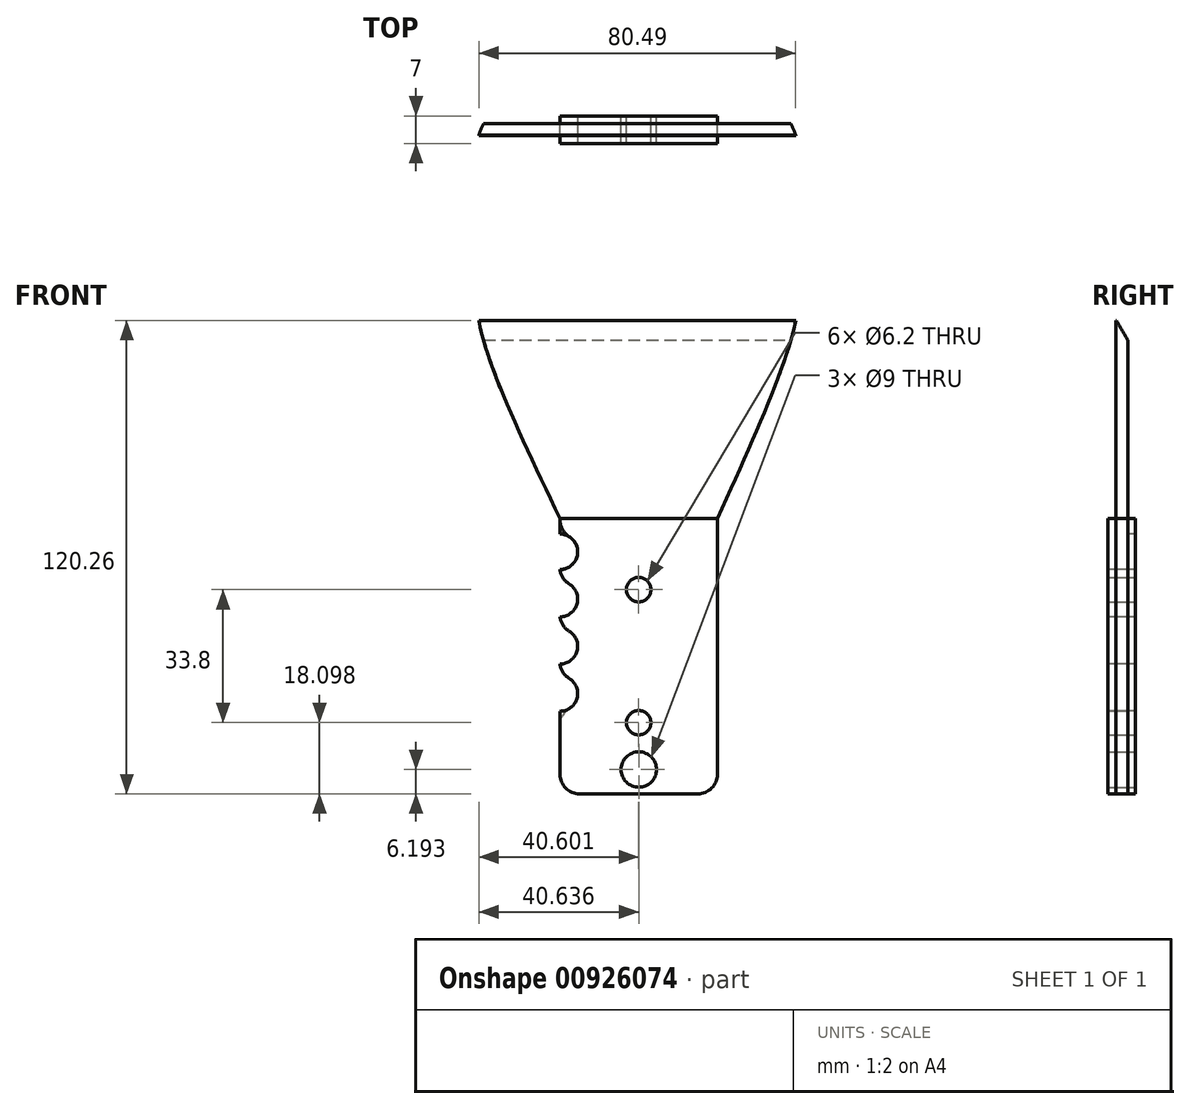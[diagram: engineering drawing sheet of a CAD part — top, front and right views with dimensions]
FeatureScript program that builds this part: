
annotation { "Feature Type Name" : "Feature", "Feature Type Description" : "" }
export const myFeature = defineFeature(function(context is Context, id is Id, definition is map)
    precondition{}
    {
        {
            var Q0;
            Q0=qCreatedBy(makeId("Front.planeOp"),FACE);
            var sketch = newSketch(context, id + "F0", { "sketchPlane" : qUnion([Q0])});
            skLineSegment(sketch, "E0.bottom", {"start": v(-37.72, -65.67) * mm, "end": v(2.28, -65.67) * mm});
            skLineSegment(sketch, "E0.top", {"start": v(-37.72, 4.33) * mm, "end": v(2.28, 4.33) * mm});
            skLineSegment(sketch, "E0.left", {"start": v(-37.72, -65.67) * mm, "end": v(-37.72, 4.33) * mm});
            skLineSegment(sketch, "E0.right", {"start": v(2.28, -65.67) * mm, "end": v(2.28, 4.33) * mm});
            skFitSpline(sketch, "E1", {"points": [v(-37.72, 4.33) * mm, v(-58.32, 54.6) * mm, v(-57.84, 68.97) * mm], "startDerivative": vector(-41.97, 87.3) * mm, "endDerivative": vector(6.95, 36.57) * mm});
            skFitSpline(sketch, "E2", {"points": [v(2.28, 4.33) * mm, v(22.17, 54.6) * mm, v(22.41, 68) * mm], "startDerivative": vector(39.5, 86.98) * mm, "endDerivative": vector(-4.12, 34.53) * mm});
            skLineSegment(sketch, "E3", {"start": v(-58.32, 54.6) * mm, "end": v(22.17, 54.6) * mm});
            skSolve(sketch);
        }
        {
            var Q0;
            Q0 = qSketchRegion(id + "F0", true);
            extrude(context, id + "F1", {"entities" : qUnion([Q0]), "depth" : 3 * mm, "offsetDistance" : 25 * mm});
        }
        {
            var Q0;
            Q0=makeQuery(id+"F1.opExtrude","CAP_EDGE",EDGE,{"disambiguationData":[OSD([sQuery(id+"F0.wireOp",EDGE,"E3")])],"isStart":true});
            chamfer(context, id + "F2", {"entities" : qUnion([Q0]), "chamferType" : ChamferType.OFFSET_ANGLE, "width" : 5 * mm, "oppositeDirection" : false, "angle" : 30 * degree, "tangentPropagation" : true});
        }
        {
            var Q0;
            Q0=makeQuery(id+"F1.opExtrude","SWEPT_EDGE",EDGE,{"disambiguationData":[OSD([sQuery(id+"F0.wireOp",EDGE,"E0.bottom"),sQuery(id+"F0.wireOp",EDGE,"E0.right")])]});
            var Q1;
            Q1=makeQuery(id+"F1.opExtrude","SWEPT_EDGE",EDGE,{"disambiguationData":[OSD([sQuery(id+"F0.wireOp",EDGE,"E0.bottom"),sQuery(id+"F0.wireOp",EDGE,"E0.left")])]});
            fillet(context, id + "F3", {"entities" : qUnion([Q0, Q1]), "radius" : 5 * mm, "tangentPropagation" : true, "allowEdgeOverflow" : false});
        }
        {
            var Q0;
            Q0=makeQuery(id+"F1.opExtrude","CAP_FACE",FACE,{"disambiguationData":[OSD([sQuery(id+"F0.wireOp",EDGE,"E0.bottom"),sQuery(id+"F0.wireOp",EDGE,"E0.left"),sQuery(id+"F0.wireOp",EDGE,"E0.right"),sQuery(id+"F0.wireOp",EDGE,"E1"),sQuery(id+"F0.wireOp",EDGE,"E2"),sQuery(id+"F0.wireOp",EDGE,"E3")])],"isStart":false});
            var sketch = newSketch(context, id + "F4", { "sketchPlane" : qUnion([Q0])});
            skLineSegment(sketch, "E4", {"start": v(-37.72, 4.33) * mm, "end": v(2.28, 4.33) * mm});
            skSolve(sketch);
        }
        {
            var Q0;
            Q0=makeQuery(id+"F4.imprint","IMPRINT",FACE,{"disambiguationData":[TD([[makeQuery(id+"F4.imprint","IMPRINT",EDGE,{"derivedFrom":sQuery(id+"F4.wireOp",EDGE,"E4")}),-1.0]])]});
            extrude(context, id + "F5", {"entities" : qUnion([Q0]), "depth" : 2 * mm, "offsetDistance" : 25 * mm});
        }
        {
            var Q0;
            Q0=makeQuery(id+"F1.opExtrude","CAP_FACE",FACE,{"disambiguationData":[OSD([sQuery(id+"F0.wireOp",EDGE,"E0.bottom"),sQuery(id+"F0.wireOp",EDGE,"E0.left"),sQuery(id+"F0.wireOp",EDGE,"E0.right"),sQuery(id+"F0.wireOp",EDGE,"E1"),sQuery(id+"F0.wireOp",EDGE,"E2"),sQuery(id+"F0.wireOp",EDGE,"E3")])],"isStart":true});
            var sketch = newSketch(context, id + "F6", { "sketchPlane" : qUnion([Q0])});
            skLineSegment(sketch, "E5", {"start": v(-2.28, 4.33) * mm, "end": v(37.72, 4.33) * mm});
            skSolve(sketch);
        }
        {
            var Q0;
            Q0=makeQuery(id+"F6.imprint","IMPRINT",FACE,{"disambiguationData":[TD([[makeQuery(id+"F6.imprint","IMPRINT",EDGE,{"derivedFrom":sQuery(id+"F6.wireOp",EDGE,"E5")}),-1.0]])]});
            extrude(context, id + "F7", {"entities" : qUnion([Q0]), "depth" : 2 * mm, "offsetDistance" : 25 * mm});
        }
        {
            var Q0;
            Q0=makeQuery(id+"F5.opExtrude","CAP_FACE",FACE,{"disambiguationData":[OSD([sQuery(id+"F0.wireOp",EDGE,"E0.bottom"),sQuery(id+"F0.wireOp",EDGE,"E0.left"),sQuery(id+"F0.wireOp",EDGE,"E0.right"),sQuery(id+"F0.wireOp",EDGE,"E1"),sQuery(id+"F0.wireOp",EDGE,"E2"),sQuery(id+"F0.wireOp",EDGE,"E3"),sQuery(id+"F4.wireOp",EDGE,"E4")])],"isStart":false});
            var sketch = newSketch(context, id + "F8", { "sketchPlane" : qUnion([Q0])});
            skCircle(sketch, "E6", {"center": v(-37.72, -4.17) * mm, "radius": 4.5 * mm});
            skCircle(sketch, "E7", {"center": v(-37.72, -16.17) * mm, "radius": 4.5 * mm});
            skCircle(sketch, "E8", {"center": v(-37.72, -28.17) * mm, "radius": 4.5 * mm});
            skCircle(sketch, "E9", {"center": v(-37.72, -40.17) * mm, "radius": 4.5 * mm});
            skSolve(sketch);
        }
        {
            var Q0;
            {var subQ0=sQuery(id+"F8.wireOp",EDGE,"E6");var subQ1=makeQuery(id+"F5.opExtrude","CAP_EDGE",EDGE,{"disambiguationData":[OSD([sQuery(id+"F0.wireOp",EDGE,"E0.left")])],"isStart":false});var subQ2=makeQuery(id+"F8.imprint","INTERSECT",VERTEX,{"disambiguationData":[OD(0.0)],"derivedFrom":[subQ1,subQ0]});Q0=makeQuery(id+"F8.imprint","IMPRINT",FACE,{"disambiguationData":[TD([[makeQuery(id+"F8.imprint","IMPRINT",EDGE,{"disambiguationData":[TD([[subQ2,1.0]])],"derivedFrom":subQ0}),1.0]])]});}
            var Q1;
            {var subQ0=sQuery(id+"F8.wireOp",EDGE,"E7");var subQ1=makeQuery(id+"F5.opExtrude","CAP_EDGE",EDGE,{"disambiguationData":[OSD([sQuery(id+"F0.wireOp",EDGE,"E0.left")])],"isStart":false});var subQ2=makeQuery(id+"F8.imprint","INTERSECT",VERTEX,{"disambiguationData":[OD(0.0)],"derivedFrom":[subQ1,subQ0]});Q1=makeQuery(id+"F8.imprint","IMPRINT",FACE,{"disambiguationData":[TD([[makeQuery(id+"F8.imprint","IMPRINT",EDGE,{"disambiguationData":[TD([[subQ2,1.0]])],"derivedFrom":subQ0}),1.0]])]});}
            var Q2;
            {var subQ0=sQuery(id+"F8.wireOp",EDGE,"E8");var subQ1=makeQuery(id+"F5.opExtrude","CAP_EDGE",EDGE,{"disambiguationData":[OSD([sQuery(id+"F0.wireOp",EDGE,"E0.left")])],"isStart":false});var subQ2=makeQuery(id+"F8.imprint","INTERSECT",VERTEX,{"disambiguationData":[OD(0.0)],"derivedFrom":[subQ1,subQ0]});Q2=makeQuery(id+"F8.imprint","IMPRINT",FACE,{"disambiguationData":[TD([[makeQuery(id+"F8.imprint","IMPRINT",EDGE,{"disambiguationData":[TD([[subQ2,-1.0]])],"derivedFrom":subQ0}),1.0]])]});}
            var Q3;
            {var subQ0=sQuery(id+"F8.wireOp",EDGE,"E9");var subQ1=makeQuery(id+"F5.opExtrude","CAP_EDGE",EDGE,{"disambiguationData":[OSD([sQuery(id+"F0.wireOp",EDGE,"E0.left")])],"isStart":false});var subQ2=makeQuery(id+"F8.imprint","INTERSECT",VERTEX,{"disambiguationData":[OD(0.0)],"derivedFrom":[subQ1,subQ0]});Q3=makeQuery(id+"F8.imprint","IMPRINT",FACE,{"disambiguationData":[TD([[makeQuery(id+"F8.imprint","IMPRINT",EDGE,{"disambiguationData":[TD([[subQ2,-1.0]])],"derivedFrom":subQ0}),1.0]])]});}
            extrude(context, id + "F9", {"entities" : qUnion([Q0, Q1, Q2, Q3]), "operationType" : NewBodyOperationType.REMOVE, "oppositeDirection" : true, "depth" : 25 * mm, "offsetDistance" : 25 * mm});
        }
        {
            var Q0;
            {var subQ0=sQuery(id+"F0.wireOp",EDGE,"E0.left");var subQ1=sQuery(id+"F8.wireOp",EDGE,"E6");Q0=makeQuery(id+"F9.boolean.opBoolean","COPY",EDGE,{"disambiguationData":[topologyDisambiguationEdgeConnected([makeQuery(id+"F5.opExtrude","SWEPT_FACE",FACE,{"disambiguationData":[OSD([subQ0])]})])],"derivedFrom":makeQuery(id+"F9.opExtrude","SWEPT_EDGE",EDGE,{"disambiguationData":[OSD([subQ0,subQ1]),TDD([makeQuery(id+"F8.imprint","INTERSECT",VERTEX,{"disambiguationData":[OD(0.0)],"derivedFrom":[makeQuery(id+"F5.opExtrude","CAP_EDGE",EDGE,{"disambiguationData":[OSD([subQ0])],"isStart":false}),subQ1]})])]})});}
            var Q1;
            {var subQ0=sQuery(id+"F0.wireOp",EDGE,"E0.left");var subQ1=sQuery(id+"F8.wireOp",EDGE,"E6");Q1=makeQuery(id+"F9.boolean.opBoolean","COPY",EDGE,{"disambiguationData":[topologyDisambiguationEdgeConnected([makeQuery(id+"F1.opExtrude","SWEPT_FACE",FACE,{"disambiguationData":[OSD([subQ0])]})])],"derivedFrom":makeQuery(id+"F9.opExtrude","SWEPT_EDGE",EDGE,{"disambiguationData":[OSD([subQ0,subQ1]),TDD([makeQuery(id+"F8.imprint","INTERSECT",VERTEX,{"disambiguationData":[OD(0.0)],"derivedFrom":[makeQuery(id+"F5.opExtrude","CAP_EDGE",EDGE,{"disambiguationData":[OSD([subQ0])],"isStart":false}),subQ1]})])]})});}
            var Q2;
            {var subQ0=sQuery(id+"F0.wireOp",EDGE,"E0.left");var subQ1=sQuery(id+"F8.wireOp",EDGE,"E6");Q2=makeQuery(id+"F9.boolean.opBoolean","COPY",EDGE,{"disambiguationData":[topologyDisambiguationEdgeConnected([makeQuery(id+"F7.opExtrude","SWEPT_FACE",FACE,{"disambiguationData":[OSD([subQ0])]})])],"derivedFrom":makeQuery(id+"F9.opExtrude","SWEPT_EDGE",EDGE,{"disambiguationData":[OSD([subQ0,subQ1]),TDD([makeQuery(id+"F8.imprint","INTERSECT",VERTEX,{"disambiguationData":[OD(0.0)],"derivedFrom":[makeQuery(id+"F5.opExtrude","CAP_EDGE",EDGE,{"disambiguationData":[OSD([subQ0])],"isStart":false}),subQ1]})])]})});}
            var Q3;
            {var subQ0=sQuery(id+"F0.wireOp",EDGE,"E0.left");var subQ1=sQuery(id+"F8.wireOp",EDGE,"E7");Q3=makeQuery(id+"F9.boolean.opBoolean","COPY",EDGE,{"disambiguationData":[topologyDisambiguationEdgeConnected([makeQuery(id+"F5.opExtrude","SWEPT_FACE",FACE,{"disambiguationData":[OSD([subQ0])]})])],"derivedFrom":makeQuery(id+"F9.opExtrude","SWEPT_EDGE",EDGE,{"disambiguationData":[OSD([subQ0,subQ1]),TDD([makeQuery(id+"F8.imprint","INTERSECT",VERTEX,{"disambiguationData":[OD(0.0)],"derivedFrom":[makeQuery(id+"F5.opExtrude","CAP_EDGE",EDGE,{"disambiguationData":[OSD([subQ0])],"isStart":false}),subQ1]})])]})});}
            var Q4;
            {var subQ0=sQuery(id+"F0.wireOp",EDGE,"E0.left");var subQ1=sQuery(id+"F8.wireOp",EDGE,"E7");Q4=makeQuery(id+"F9.boolean.opBoolean","COPY",EDGE,{"disambiguationData":[topologyDisambiguationEdgeConnected([makeQuery(id+"F1.opExtrude","SWEPT_FACE",FACE,{"disambiguationData":[OSD([subQ0])]})])],"derivedFrom":makeQuery(id+"F9.opExtrude","SWEPT_EDGE",EDGE,{"disambiguationData":[OSD([subQ0,subQ1]),TDD([makeQuery(id+"F8.imprint","INTERSECT",VERTEX,{"disambiguationData":[OD(0.0)],"derivedFrom":[makeQuery(id+"F5.opExtrude","CAP_EDGE",EDGE,{"disambiguationData":[OSD([subQ0])],"isStart":false}),subQ1]})])]})});}
            var Q5;
            {var subQ0=sQuery(id+"F0.wireOp",EDGE,"E0.left");var subQ1=sQuery(id+"F8.wireOp",EDGE,"E7");Q5=makeQuery(id+"F9.boolean.opBoolean","COPY",EDGE,{"disambiguationData":[topologyDisambiguationEdgeConnected([makeQuery(id+"F7.opExtrude","SWEPT_FACE",FACE,{"disambiguationData":[OSD([subQ0])]})])],"derivedFrom":makeQuery(id+"F9.opExtrude","SWEPT_EDGE",EDGE,{"disambiguationData":[OSD([subQ0,subQ1]),TDD([makeQuery(id+"F8.imprint","INTERSECT",VERTEX,{"disambiguationData":[OD(0.0)],"derivedFrom":[makeQuery(id+"F5.opExtrude","CAP_EDGE",EDGE,{"disambiguationData":[OSD([subQ0])],"isStart":false}),subQ1]})])]})});}
            var Q6;
            {var subQ0=sQuery(id+"F0.wireOp",EDGE,"E0.left");var subQ1=sQuery(id+"F8.wireOp",EDGE,"E8");Q6=makeQuery(id+"F9.boolean.opBoolean","COPY",EDGE,{"disambiguationData":[topologyDisambiguationEdgeConnected([makeQuery(id+"F7.opExtrude","SWEPT_FACE",FACE,{"disambiguationData":[OSD([subQ0])]})])],"derivedFrom":makeQuery(id+"F9.opExtrude","SWEPT_EDGE",EDGE,{"disambiguationData":[OSD([subQ0,subQ1]),TDD([makeQuery(id+"F8.imprint","INTERSECT",VERTEX,{"disambiguationData":[OD(1.0)],"derivedFrom":[makeQuery(id+"F5.opExtrude","CAP_EDGE",EDGE,{"disambiguationData":[OSD([subQ0])],"isStart":false}),subQ1]})])]})});}
            var Q7;
            {var subQ0=sQuery(id+"F0.wireOp",EDGE,"E0.left");var subQ1=sQuery(id+"F8.wireOp",EDGE,"E8");Q7=makeQuery(id+"F9.boolean.opBoolean","COPY",EDGE,{"disambiguationData":[topologyDisambiguationEdgeConnected([makeQuery(id+"F5.opExtrude","SWEPT_FACE",FACE,{"disambiguationData":[OSD([subQ0])]})])],"derivedFrom":makeQuery(id+"F9.opExtrude","SWEPT_EDGE",EDGE,{"disambiguationData":[OSD([subQ0,subQ1]),TDD([makeQuery(id+"F8.imprint","INTERSECT",VERTEX,{"disambiguationData":[OD(1.0)],"derivedFrom":[makeQuery(id+"F5.opExtrude","CAP_EDGE",EDGE,{"disambiguationData":[OSD([subQ0])],"isStart":false}),subQ1]})])]})});}
            var Q8;
            {var subQ0=sQuery(id+"F0.wireOp",EDGE,"E0.left");var subQ1=sQuery(id+"F8.wireOp",EDGE,"E8");Q8=makeQuery(id+"F9.boolean.opBoolean","COPY",EDGE,{"disambiguationData":[topologyDisambiguationEdgeConnected([makeQuery(id+"F1.opExtrude","SWEPT_FACE",FACE,{"disambiguationData":[OSD([subQ0])]})])],"derivedFrom":makeQuery(id+"F9.opExtrude","SWEPT_EDGE",EDGE,{"disambiguationData":[OSD([subQ0,subQ1]),TDD([makeQuery(id+"F8.imprint","INTERSECT",VERTEX,{"disambiguationData":[OD(1.0)],"derivedFrom":[makeQuery(id+"F5.opExtrude","CAP_EDGE",EDGE,{"disambiguationData":[OSD([subQ0])],"isStart":false}),subQ1]})])]})});}
            var Q9;
            {var subQ0=sQuery(id+"F0.wireOp",EDGE,"E0.left");var subQ1=sQuery(id+"F8.wireOp",EDGE,"E9");Q9=makeQuery(id+"F9.boolean.opBoolean","COPY",EDGE,{"disambiguationData":[topologyDisambiguationEdgeConnected([makeQuery(id+"F1.opExtrude","SWEPT_FACE",FACE,{"disambiguationData":[OSD([subQ0])]})])],"derivedFrom":makeQuery(id+"F9.opExtrude","SWEPT_EDGE",EDGE,{"disambiguationData":[OSD([subQ0,subQ1]),TDD([makeQuery(id+"F8.imprint","INTERSECT",VERTEX,{"disambiguationData":[OD(1.0)],"derivedFrom":[makeQuery(id+"F5.opExtrude","CAP_EDGE",EDGE,{"disambiguationData":[OSD([subQ0])],"isStart":false}),subQ1]})])]})});}
            var Q10;
            {var subQ0=sQuery(id+"F0.wireOp",EDGE,"E0.left");var subQ1=sQuery(id+"F8.wireOp",EDGE,"E9");Q10=makeQuery(id+"F9.boolean.opBoolean","COPY",EDGE,{"disambiguationData":[topologyDisambiguationEdgeConnected([makeQuery(id+"F7.opExtrude","SWEPT_FACE",FACE,{"disambiguationData":[OSD([subQ0])]})])],"derivedFrom":makeQuery(id+"F9.opExtrude","SWEPT_EDGE",EDGE,{"disambiguationData":[OSD([subQ0,subQ1]),TDD([makeQuery(id+"F8.imprint","INTERSECT",VERTEX,{"disambiguationData":[OD(1.0)],"derivedFrom":[makeQuery(id+"F5.opExtrude","CAP_EDGE",EDGE,{"disambiguationData":[OSD([subQ0])],"isStart":false}),subQ1]})])]})});}
            var Q11;
            {var subQ0=sQuery(id+"F0.wireOp",EDGE,"E0.left");var subQ1=sQuery(id+"F8.wireOp",EDGE,"E9");Q11=makeQuery(id+"F9.boolean.opBoolean","COPY",EDGE,{"disambiguationData":[topologyDisambiguationEdgeConnected([makeQuery(id+"F5.opExtrude","SWEPT_FACE",FACE,{"disambiguationData":[OSD([subQ0])]})])],"derivedFrom":makeQuery(id+"F9.opExtrude","SWEPT_EDGE",EDGE,{"disambiguationData":[OSD([subQ0,subQ1]),TDD([makeQuery(id+"F8.imprint","INTERSECT",VERTEX,{"disambiguationData":[OD(1.0)],"derivedFrom":[makeQuery(id+"F5.opExtrude","CAP_EDGE",EDGE,{"disambiguationData":[OSD([subQ0])],"isStart":false}),subQ1]})])]})});}
            var Q12;
            {var subQ0=sQuery(id+"F0.wireOp",EDGE,"E0.left");var subQ1=sQuery(id+"F8.wireOp",EDGE,"E9");Q12=makeQuery(id+"F9.boolean.opBoolean","COPY",EDGE,{"disambiguationData":[topologyDisambiguationEdgeConnected([makeQuery(id+"F5.opExtrude","SWEPT_FACE",FACE,{"disambiguationData":[OSD([subQ0])]})])],"derivedFrom":makeQuery(id+"F9.opExtrude","SWEPT_EDGE",EDGE,{"disambiguationData":[OSD([subQ0,subQ1]),TDD([makeQuery(id+"F8.imprint","INTERSECT",VERTEX,{"disambiguationData":[OD(0.0)],"derivedFrom":[makeQuery(id+"F5.opExtrude","CAP_EDGE",EDGE,{"disambiguationData":[OSD([subQ0])],"isStart":false}),subQ1]})])]})});}
            var Q13;
            {var subQ0=sQuery(id+"F0.wireOp",EDGE,"E0.left");var subQ1=sQuery(id+"F8.wireOp",EDGE,"E9");Q13=makeQuery(id+"F9.boolean.opBoolean","COPY",EDGE,{"disambiguationData":[topologyDisambiguationEdgeConnected([makeQuery(id+"F1.opExtrude","SWEPT_FACE",FACE,{"disambiguationData":[OSD([subQ0])]})])],"derivedFrom":makeQuery(id+"F9.opExtrude","SWEPT_EDGE",EDGE,{"disambiguationData":[OSD([subQ0,subQ1]),TDD([makeQuery(id+"F8.imprint","INTERSECT",VERTEX,{"disambiguationData":[OD(0.0)],"derivedFrom":[makeQuery(id+"F5.opExtrude","CAP_EDGE",EDGE,{"disambiguationData":[OSD([subQ0])],"isStart":false}),subQ1]})])]})});}
            var Q14;
            {var subQ0=sQuery(id+"F0.wireOp",EDGE,"E0.left");var subQ1=sQuery(id+"F8.wireOp",EDGE,"E9");Q14=makeQuery(id+"F9.boolean.opBoolean","COPY",EDGE,{"disambiguationData":[topologyDisambiguationEdgeConnected([makeQuery(id+"F7.opExtrude","SWEPT_FACE",FACE,{"disambiguationData":[OSD([subQ0])]})])],"derivedFrom":makeQuery(id+"F9.opExtrude","SWEPT_EDGE",EDGE,{"disambiguationData":[OSD([subQ0,subQ1]),TDD([makeQuery(id+"F8.imprint","INTERSECT",VERTEX,{"disambiguationData":[OD(0.0)],"derivedFrom":[makeQuery(id+"F5.opExtrude","CAP_EDGE",EDGE,{"disambiguationData":[OSD([subQ0])],"isStart":false}),subQ1]})])]})});}
            fillet(context, id + "F10", {"entities" : qUnion([Q0, Q1, Q2, Q3, Q4, Q5, Q6, Q7, Q8, Q9, Q10, Q11, Q12, Q13, Q14]), "radius" : 5 * mm, "tangentPropagation" : true, "allowEdgeOverflow" : false});
        }
        {
            var Q0;
            Q0=makeQuery(id+"F7.opExtrude","CAP_FACE",FACE,{"disambiguationData":[OSD([sQuery(id+"F0.wireOp",EDGE,"E0.bottom"),sQuery(id+"F0.wireOp",EDGE,"E0.left"),sQuery(id+"F0.wireOp",EDGE,"E0.right"),sQuery(id+"F0.wireOp",EDGE,"E1"),sQuery(id+"F0.wireOp",EDGE,"E2"),sQuery(id+"F0.wireOp",EDGE,"E3"),sQuery(id+"F6.wireOp",EDGE,"E5")])],"isStart":false});
            var sketch = newSketch(context, id + "F11", { "sketchPlane" : qUnion([Q0])});
            skCircle(sketch, "E10", {"center": v(17.72, -47.57) * mm, "radius": 3.1 * mm});
            skCircle(sketch, "E11", {"center": v(17.72, -13.77) * mm, "radius": 3.1 * mm});
            skLineSegment(sketch, "E12", {"start": v(-2.28, 4.33) * mm, "end": v(37.72, 4.33) * mm});
            skSolve(sketch);
        }
        {
            var Q0;
            Q0=makeQuery(id+"F11.imprint","IMPRINT",FACE,{"disambiguationData":[TD([[makeQuery(id+"F11.imprint","IMPRINT",EDGE,{"derivedFrom":sQuery(id+"F11.wireOp",EDGE,"E11")}),1.0]])]});
            var Q1;
            Q1=makeQuery(id+"F11.imprint","IMPRINT",FACE,{"disambiguationData":[TD([[makeQuery(id+"F11.imprint","IMPRINT",EDGE,{"derivedFrom":sQuery(id+"F11.wireOp",EDGE,"E10")}),1.0]])]});
            extrude(context, id + "F12", {"entities" : qUnion([Q0, Q1]), "operationType" : NewBodyOperationType.REMOVE, "oppositeDirection" : true, "depth" : 25 * mm, "offsetDistance" : 25 * mm});
        }
        {
            var Q0;
            Q0=makeQuery(id+"F7.opExtrude","CAP_FACE",FACE,{"disambiguationData":[OSD([sQuery(id+"F0.wireOp",EDGE,"E0.bottom"),sQuery(id+"F0.wireOp",EDGE,"E0.left"),sQuery(id+"F0.wireOp",EDGE,"E0.right"),sQuery(id+"F0.wireOp",EDGE,"E1"),sQuery(id+"F0.wireOp",EDGE,"E2"),sQuery(id+"F0.wireOp",EDGE,"E3"),sQuery(id+"F6.wireOp",EDGE,"E5")])],"isStart":false});
            var sketch = newSketch(context, id + "F13", { "sketchPlane" : qUnion([Q0])});
            skCircle(sketch, "E13", {"center": v(17.68, -59.48) * mm, "radius": 4.5 * mm});
            skSolve(sketch);
        }
        {
            var Q0;
            Q0=makeQuery(id+"F13.imprint","IMPRINT",FACE,{"disambiguationData":[TD([[makeQuery(id+"F13.imprint","IMPRINT",EDGE,{"derivedFrom":sQuery(id+"F13.wireOp",EDGE,"E13")}),1.0]])]});
            extrude(context, id + "F14", {"entities" : qUnion([Q0]), "operationType" : NewBodyOperationType.REMOVE, "oppositeDirection" : true, "depth" : 25 * mm, "offsetDistance" : 25 * mm});
        }
    });
